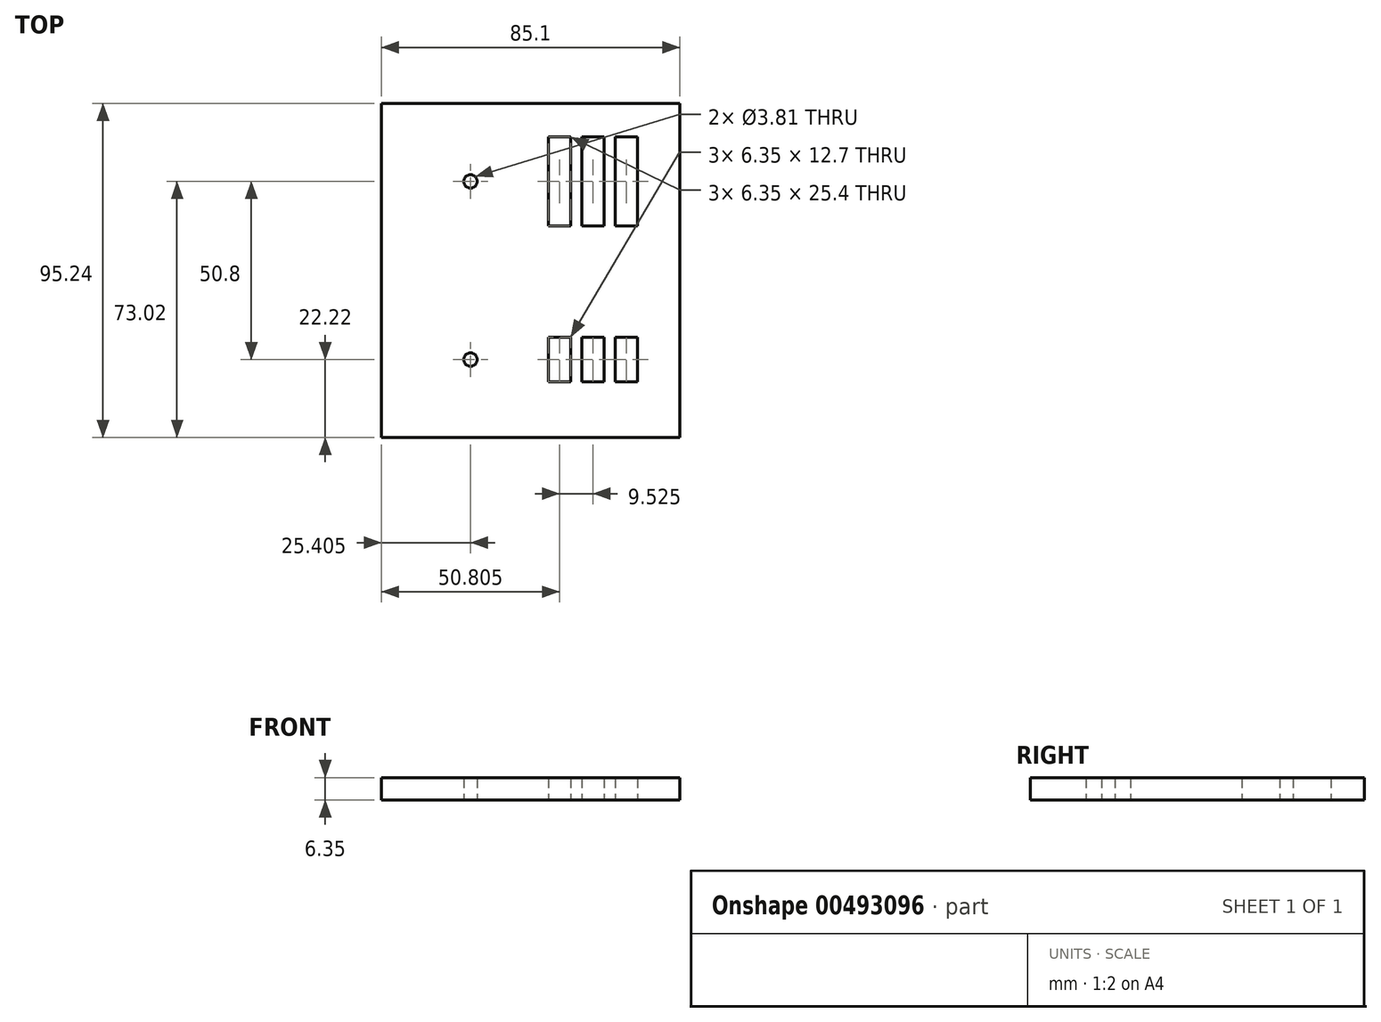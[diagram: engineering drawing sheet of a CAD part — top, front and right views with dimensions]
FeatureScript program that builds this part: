
annotation { "Feature Type Name" : "Feature", "Feature Type Description" : "" }
export const myFeature = defineFeature(function(context is Context, id is Id, definition is map)
    precondition{}
    {
        {
            var Q0;
            Q0=qCreatedBy(makeId("Top.planeOp"),FACE);
            var sketch = newSketch(context, id + "F0", { "sketchPlane" : qUnion([Q0])});
            skLineSegment(sketch, "E0.bottom", {"start": v(-42.55, 47.63) * mm, "end": v(42.55, 47.63) * mm});
            skLineSegment(sketch, "E0.top", {"start": v(-42.55, -47.63) * mm, "end": v(42.55, -47.63) * mm});
            skLineSegment(sketch, "E0.left", {"start": v(-42.55, 47.63) * mm, "end": v(-42.55, -47.63) * mm});
            skLineSegment(sketch, "E0.right", {"start": v(42.55, 47.63) * mm, "end": v(42.55, -47.63) * mm});
            skPoint(sketch, "E0.middle", {"position": v(0, 0) * mm});
            skSolve(sketch);
        }
        {
            var Q0;
            Q0=qSketchRegion(id+"F0",true);
            extrude(context, id + "F1", {"entities" : qUnion([Q0]), "depth" : 6.35 * mm});
        }
        {
            var Q0;
            Q0=qCreatedBy(makeId("Top.planeOp"),FACE);
            var sketch = newSketch(context, id + "F2", { "sketchPlane" : qUnion([Q0])});
            skCircle(sketch, "E1", {"center": v(-17.15, -25.4) * mm, "radius": 1.9 * mm});
            skCircle(sketch, "E2.0.1.0", {"center": v(-17.15, 25.4) * mm, "radius": 1.9 * mm});
            skLineSegment(sketch, "E2.direction1", {"start": v(-17.15, -25.4) * mm, "end": v(6.38, -25.4) * mm, "construction": true});
            skLineSegment(sketch, "E2.direction2", {"start": v(-17.15, -25.4) * mm, "end": v(-17.15, 25.4) * mm, "construction": true});
            skLineSegment(sketch, "E3.bottom", {"start": v(5.08, -19.05) * mm, "end": v(11.43, -19.05) * mm});
            skLineSegment(sketch, "E3.top", {"start": v(5.08, -31.75) * mm, "end": v(11.43, -31.75) * mm});
            skLineSegment(sketch, "E3.left", {"start": v(5.08, -19.05) * mm, "end": v(5.08, -31.75) * mm});
            skLineSegment(sketch, "E3.right", {"start": v(11.43, -19.05) * mm, "end": v(11.43, -31.75) * mm});
            skPoint(sketch, "E3.middle", {"position": v(8.25, -25.4) * mm});
            skLineSegment(sketch, "E4.bottom", {"start": v(5.08, 31.75) * mm, "end": v(11.43, 31.75) * mm});
            skLineSegment(sketch, "E4.top", {"start": v(5.08, 19.05) * mm, "end": v(11.43, 19.05) * mm});
            skLineSegment(sketch, "E4.left", {"start": v(5.08, 31.75) * mm, "end": v(5.08, 19.05) * mm});
            skLineSegment(sketch, "E4.right", {"start": v(11.43, 31.75) * mm, "end": v(11.43, 19.05) * mm});
            skPoint(sketch, "E4.middle", {"position": v(8.25, 25.4) * mm});
            skLineSegment(sketch, "E5.1.0.0", {"start": v(30.48, 31.75) * mm, "end": v(30.48, 19.05) * mm});
            skLineSegment(sketch, "E5.1.0.1", {"start": v(24.13, 19.05) * mm, "end": v(30.48, 19.05) * mm});
            skLineSegment(sketch, "E5.1.0.2", {"start": v(24.13, 31.75) * mm, "end": v(24.13, 19.05) * mm});
            skLineSegment(sketch, "E5.1.0.3", {"start": v(24.13, -19.05) * mm, "end": v(30.48, -19.05) * mm});
            skLineSegment(sketch, "E5.1.0.4", {"start": v(30.48, -19.05) * mm, "end": v(30.48, -31.75) * mm});
            skLineSegment(sketch, "E5.1.0.5", {"start": v(24.13, -19.05) * mm, "end": v(24.13, -31.75) * mm});
            skLineSegment(sketch, "E5.1.0.6", {"start": v(24.13, -31.75) * mm, "end": v(30.48, -31.75) * mm});
            skLineSegment(sketch, "E5.direction1", {"start": v(11.43, 19.05) * mm, "end": v(30.48, 19.05) * mm, "construction": true});
            skLineSegment(sketch, "E6", {"start": v(-17.15, 25.4) * mm, "end": v(-17.15, -25.4) * mm, "construction": true});
            skPoint(sketch, "E7", {"position": v(-17.15, 0) * mm});
            skLineSegment(sketch, "E8", {"start": v(24.13, 31.75) * mm, "end": v(30.48, 31.75) * mm});
            skLineSegment(sketch, "E9", {"start": v(11.43, 25.4) * mm, "end": v(24.13, 25.4) * mm, "construction": true});
            skLineSegment(sketch, "E10", {"start": v(11.43, -25.4) * mm, "end": v(24.13, -25.4) * mm, "construction": true});
            skLineSegment(sketch, "E11.bottom", {"start": v(14.6, 31.75) * mm, "end": v(20.95, 31.75) * mm});
            skLineSegment(sketch, "E11.top", {"start": v(14.6, 19.05) * mm, "end": v(20.95, 19.05) * mm});
            skLineSegment(sketch, "E11.left", {"start": v(14.6, 31.75) * mm, "end": v(14.6, 19.05) * mm});
            skLineSegment(sketch, "E11.right", {"start": v(20.95, 31.75) * mm, "end": v(20.95, 19.05) * mm});
            skPoint(sketch, "E11.middle", {"position": v(17.78, 25.4) * mm});
            skLineSegment(sketch, "E12.bottom", {"start": v(14.6, -19.05) * mm, "end": v(20.95, -19.05) * mm});
            skLineSegment(sketch, "E12.top", {"start": v(14.6, -31.75) * mm, "end": v(20.95, -31.75) * mm});
            skLineSegment(sketch, "E12.left", {"start": v(14.6, -19.05) * mm, "end": v(14.6, -31.75) * mm});
            skLineSegment(sketch, "E12.right", {"start": v(20.96, -19.05) * mm, "end": v(20.96, -31.75) * mm});
            skPoint(sketch, "E12.middle", {"position": v(17.78, -25.4) * mm});
            skLineSegment(sketch, "E13.bottom", {"start": v(5.08, 38.1) * mm, "end": v(11.43, 38.1) * mm});
            skLineSegment(sketch, "E13.top", {"start": v(5.08, 12.7) * mm, "end": v(11.43, 12.7) * mm});
            skLineSegment(sketch, "E13.left", {"start": v(5.08, 38.1) * mm, "end": v(5.08, 12.7) * mm});
            skLineSegment(sketch, "E13.right", {"start": v(11.43, 38.1) * mm, "end": v(11.43, 12.7) * mm});
            skLineSegment(sketch, "E14.bottom", {"start": v(14.6, 38.1) * mm, "end": v(20.95, 38.1) * mm});
            skLineSegment(sketch, "E14.top", {"start": v(14.6, 12.7) * mm, "end": v(20.95, 12.7) * mm});
            skLineSegment(sketch, "E14.left", {"start": v(14.6, 38.1) * mm, "end": v(14.6, 12.7) * mm});
            skLineSegment(sketch, "E14.right", {"start": v(20.95, 38.1) * mm, "end": v(20.95, 12.7) * mm});
            skLineSegment(sketch, "E15", {"start": v(24.13, 25.4) * mm, "end": v(30.48, 25.4) * mm, "construction": true});
            skPoint(sketch, "E16", {"position": v(27.3, 25.4) * mm});
            skLineSegment(sketch, "E17", {"start": v(24.13, 12.7) * mm, "end": v(30.48, 12.7) * mm});
            skLineSegment(sketch, "E18", {"start": v(30.48, 12.7) * mm, "end": v(30.48, 38.1) * mm});
            skLineSegment(sketch, "E19", {"start": v(30.48, 38.1) * mm, "end": v(24.13, 38.1) * mm});
            skLineSegment(sketch, "E20", {"start": v(24.13, 38.1) * mm, "end": v(24.13, 12.7) * mm});
            skSolve(sketch);
        }
        {
            var Q0;
            Q0=qSketchRegion(id+"F2",true);
            extrude(context, id + "F3", {"entities" : qUnion([Q0]), "operationType" : NewBodyOperationType.REMOVE, "endBound" : BoundingType.THROUGH_ALL, "depth" : 25.4 * mm});
        }
        {
            var Q0;
            Q0 = qSketchRegion(id + "F2", true);
            extrude(context, id + "F4", {"entities" : qUnion([Q0]), "operationType" : NewBodyOperationType.REMOVE, "endBound" : BoundingType.THROUGH_ALL, "oppositeDirection" : true, "depth" : 25.4 * mm});
        }
    });
